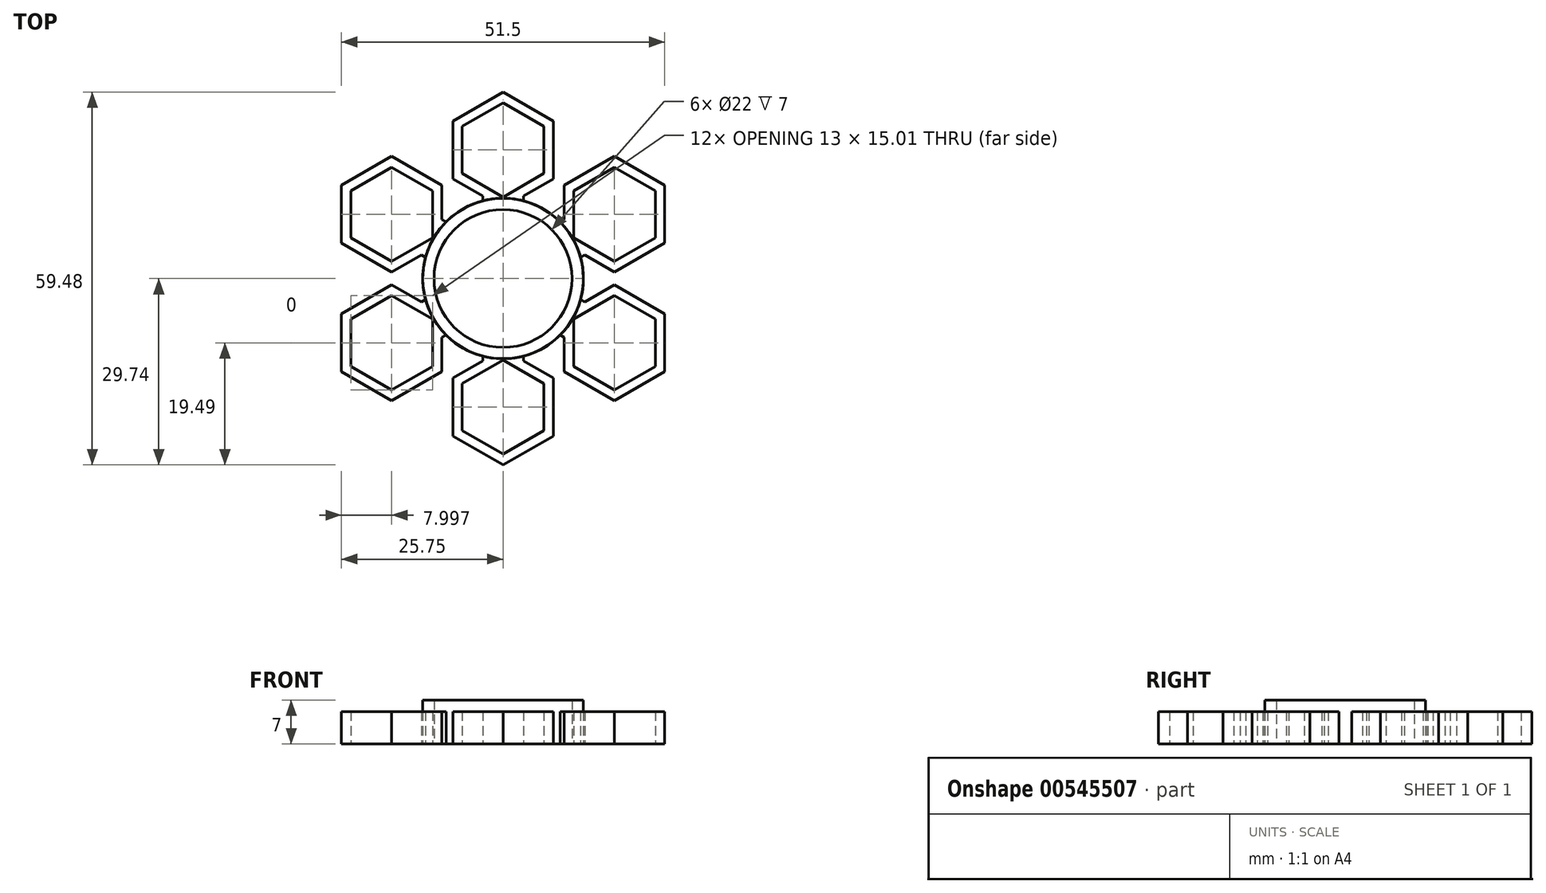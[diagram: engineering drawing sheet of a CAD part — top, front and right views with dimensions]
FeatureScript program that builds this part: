
annotation { "Feature Type Name" : "Feature", "Feature Type Description" : "" }
export const myFeature = defineFeature(function(context is Context, id is Id, definition is map)
    precondition{}
    {
        {
            var Q0;
            Q0=qCreatedBy(makeId("Top.planeOp"),FACE);
            var sketch = newSketch(context, id + "F0", { "sketchPlane" : qUnion([Q0])});
            skCircle(sketch, "E0", {"center": v(0, 0) * mm, "radius": 30 * mm});
            skCircle(sketch, "E1", {"center": v(0, 0) * mm, "radius": 11 * mm});
            skLineSegment(sketch, "E2", {"start": v(0, 20.5) * mm, "end": v(6.5, 20.5) * mm});
            skPoint(sketch, "E2.endSnap0", {"position": v(0, 20.5) * mm});
            skLineSegment(sketch, "E3", {"start": v(0, 20.5) * mm, "end": v(-6.5, 20.5) * mm});
            skCircle(sketch, "E4.cCircle", {"center": v(0, 20.5) * mm, "radius": 6.5 * mm, "construction": true});
            skLineSegment(sketch, "E4.0", {"start": v(-6.5, 16.75) * mm, "end": v(-6.5, 24.25) * mm});
            skLineSegment(sketch, "E4.1", {"start": v(-6.5, 24.25) * mm, "end": v(0, 28) * mm});
            skLineSegment(sketch, "E4.2", {"start": v(0, 28) * mm, "end": v(6.5, 24.25) * mm});
            skLineSegment(sketch, "E4.3", {"start": v(6.5, 24.25) * mm, "end": v(6.5, 16.75) * mm});
            skLineSegment(sketch, "E4.4", {"start": v(6.5, 16.75) * mm, "end": v(0, 13) * mm});
            skLineSegment(sketch, "E4.5", {"start": v(0, 13) * mm, "end": v(-6.5, 16.75) * mm});
            skPoint(sketch, "E4.0.midPoint", {"position": v(-6.5, 20.5) * mm});
            skLineSegment(sketch, "E5.MirrorCS", {"start": v(0, 35.51) * mm, "end": v(0, 28) * mm});
            skLineSegment(sketch, "E6.MirrorCS", {"start": v(6.5, -24.25) * mm, "end": v(6.5, -16.75) * mm});
            skLineSegment(sketch, "E7.MirrorCS", {"start": v(6.5, -16.75) * mm, "end": v(0, -13) * mm});
            skLineSegment(sketch, "E8.MirrorCS", {"start": v(0, -13) * mm, "end": v(-6.5, -16.75) * mm});
            skLineSegment(sketch, "E9.MirrorCS", {"start": v(-6.5, -16.75) * mm, "end": v(-6.5, -24.25) * mm});
            skLineSegment(sketch, "E10.MirrorCS", {"start": v(-6.5, -24.25) * mm, "end": v(0, -28) * mm});
            skLineSegment(sketch, "E11.MirrorCS", {"start": v(0, -28) * mm, "end": v(6.5, -24.25) * mm});
            skLineSegment(sketch, "E12", {"start": v(-3.25, 14.87) * mm, "end": v(-3.25, 10.5) * mm});
            skLineSegment(sketch, "E13", {"start": v(3.25, 13.14) * mm, "end": v(3.25, 12.38) * mm});
            skLineSegment(sketch, "E14", {"start": v(-3.25, -13.14) * mm, "end": v(-3.25, -12.38) * mm});
            skLineSegment(sketch, "E15", {"start": v(3.25, -13.14) * mm, "end": v(3.25, -12.38) * mm});
            skLineSegment(sketch, "E16.0", {"start": v(8, -15.88) * mm, "end": v(3.25, -13.14) * mm});
            skLineSegment(sketch, "E16.1", {"start": v(-8, -15.88) * mm, "end": v(-8, -25.12) * mm});
            skLineSegment(sketch, "E16.2", {"start": v(-8, -25.12) * mm, "end": v(0, -29.74) * mm});
            skLineSegment(sketch, "E16.4", {"start": v(0, -29.74) * mm, "end": v(8, -25.12) * mm});
            skLineSegment(sketch, "E16.5", {"start": v(8, -25.12) * mm, "end": v(8, -15.88) * mm});
            skLineSegment(sketch, "E17.0", {"start": v(-3.25, 13.14) * mm, "end": v(-8, 15.88) * mm});
            skLineSegment(sketch, "E17.1", {"start": v(-8, 25.12) * mm, "end": v(0, 29.74) * mm});
            skLineSegment(sketch, "E17.2", {"start": v(0, 29.74) * mm, "end": v(8, 25.12) * mm});
            skLineSegment(sketch, "E17.3", {"start": v(-8, 15.88) * mm, "end": v(-8, 25.12) * mm});
            skLineSegment(sketch, "E17.4", {"start": v(8, 25.12) * mm, "end": v(8, 15.88) * mm});
            skLineSegment(sketch, "E17.5", {"start": v(8, 15.88) * mm, "end": v(3.25, 13.14) * mm});
            skArc(sketch, "E18.0", {"start": v(-3.25, 12.38) * mm, "mid": v(-12.8, 0) * mm, "end": v(-3.25, -12.38) * mm});
            skArc(sketch, "E19.trimOffspring", {"start": v(3.25, -12.38) * mm, "mid": v(12.8, 0) * mm, "end": v(3.25, 12.38) * mm});
            skLineSegment(sketch, "E20.trimOffspring", {"start": v(-3.25, -13.14) * mm, "end": v(-8, -15.88) * mm});
            skPoint(sketch, "E21.orphan", {"position": v(-3.25, -14.87) * mm});
            skPoint(sketch, "E22.orphan", {"position": v(3.25, -14.87) * mm});
            skLineSegment(sketch, "E23.trimOffspring", {"start": v(0, 12.8) * mm, "end": v(0, 30) * mm});
            skPoint(sketch, "E24.start.orphan", {"position": v(0, 11) * mm});
            skPoint(sketch, "E25.orphan", {"position": v(3.25, 14.87) * mm});
            skSolve(sketch);
        }
        {
            var Q0;
            Q0=makeQuery(id+"F0.imprint","IMPRINT",FACE,{"disambiguationData":[TD([[makeQuery(id+"F0.imprint","IMPRINT",EDGE,{"derivedFrom":sQuery(id+"F0.wireOp",EDGE,"E1")}),-1.0]])]});
            var Q1;
            {var subQ5=sQuery(id+"F0.wireOp",EDGE,"E4.1");Q1=makeQuery(id+"F0.imprint","IMPRINT",FACE,{"disambiguationData":[TD([[makeQuery(id+"F0.imprint","IMPRINT",EDGE,{"derivedFrom":subQ5}),1.0]])]});}
            extrude(context, id + "F1", {"entities" : qUnion([Q0, Q1]), "depth" : 7 * mm, "offsetDistance" : 25 * mm});
        }
        {
            var Q0;
            Q0=makeQuery(id+"F1.opExtrude","CAP_FACE",FACE,{"disambiguationData":[OSD([sQuery(id+"F0.wireOp",EDGE,"E1"),sQuery(id+"F0.wireOp",EDGE,"E4.0"),sQuery(id+"F0.wireOp",EDGE,"E4.1"),sQuery(id+"F0.wireOp",EDGE,"E4.2"),sQuery(id+"F0.wireOp",EDGE,"E4.3"),sQuery(id+"F0.wireOp",EDGE,"E4.4"),sQuery(id+"F0.wireOp",EDGE,"E4.5"),sQuery(id+"F0.wireOp",EDGE,"E6.MirrorCS"),sQuery(id+"F0.wireOp",EDGE,"E7.MirrorCS"),sQuery(id+"F0.wireOp",EDGE,"E8.MirrorCS"),sQuery(id+"F0.wireOp",EDGE,"E9.MirrorCS"),sQuery(id+"F0.wireOp",EDGE,"E10.MirrorCS"),sQuery(id+"F0.wireOp",EDGE,"E11.MirrorCS"),sQuery(id+"F0.wireOp",EDGE,"E12"),sQuery(id+"F0.wireOp",EDGE,"E13"),sQuery(id+"F0.wireOp",EDGE,"E14"),sQuery(id+"F0.wireOp",EDGE,"E15"),sQuery(id+"F0.wireOp",EDGE,"E16.0"),sQuery(id+"F0.wireOp",EDGE,"E16.1"),sQuery(id+"F0.wireOp",EDGE,"E16.2"),sQuery(id+"F0.wireOp",EDGE,"E16.4"),sQuery(id+"F0.wireOp",EDGE,"E16.5"),sQuery(id+"F0.wireOp",EDGE,"E17.0"),sQuery(id+"F0.wireOp",EDGE,"E17.1"),sQuery(id+"F0.wireOp",EDGE,"E17.2"),sQuery(id+"F0.wireOp",EDGE,"E17.3"),sQuery(id+"F0.wireOp",EDGE,"E17.4"),sQuery(id+"F0.wireOp",EDGE,"E17.5"),sQuery(id+"F0.wireOp",EDGE,"E18.0"),sQuery(id+"F0.wireOp",EDGE,"E19.trimOffspring"),sQuery(id+"F0.wireOp",EDGE,"E20.trimOffspring")])],"isStart":false});
            var sketch = newSketch(context, id + "F2", { "sketchPlane" : qUnion([Q0])});
            skArc(sketch, "E26", {"start": v(-3.25, 12.38) * mm, "mid": v(0, 12.8) * mm, "end": v(3.25, 12.38) * mm});
            skLineSegment(sketch, "E27", {"start": v(-3.25, 12.38) * mm, "end": v(-3.25, 13.14) * mm});
            skLineSegment(sketch, "E28", {"start": v(-3.25, 13.14) * mm, "end": v(-8, 15.88) * mm});
            skLineSegment(sketch, "E29", {"start": v(-8, 15.88) * mm, "end": v(-8, 25.12) * mm});
            skLineSegment(sketch, "E30", {"start": v(-8, 25.12) * mm, "end": v(0, 29.74) * mm});
            skLineSegment(sketch, "E31", {"start": v(0, 29.74) * mm, "end": v(8, 25.12) * mm});
            skLineSegment(sketch, "E32", {"start": v(8, 25.12) * mm, "end": v(8, 15.88) * mm});
            skLineSegment(sketch, "E33", {"start": v(8, 15.88) * mm, "end": v(3.25, 13.14) * mm});
            skLineSegment(sketch, "E34", {"start": v(3.25, 13.14) * mm, "end": v(3.25, 12.38) * mm});
            skLineSegment(sketch, "E35", {"start": v(0, 13) * mm, "end": v(-6.5, 16.75) * mm});
            skLineSegment(sketch, "E36", {"start": v(-6.5, 16.75) * mm, "end": v(-6.5, 24.25) * mm});
            skLineSegment(sketch, "E37", {"start": v(-6.5, 24.25) * mm, "end": v(0, 28) * mm});
            skLineSegment(sketch, "E38", {"start": v(0, 28) * mm, "end": v(6.5, 24.25) * mm});
            skLineSegment(sketch, "E39", {"start": v(6.5, 24.25) * mm, "end": v(6.5, 16.75) * mm});
            skLineSegment(sketch, "E40", {"start": v(6.5, 16.75) * mm, "end": v(0, 13) * mm});
            skArc(sketch, "E41", {"start": v(-3.25, -12.38) * mm, "mid": v(0, -12.8) * mm, "end": v(3.25, -12.38) * mm});
            skLineSegment(sketch, "E42", {"start": v(3.25, -12.38) * mm, "end": v(3.25, -13.14) * mm});
            skLineSegment(sketch, "E43", {"start": v(3.25, -13.14) * mm, "end": v(8, -15.88) * mm});
            skLineSegment(sketch, "E44", {"start": v(8, -15.88) * mm, "end": v(8, -25.12) * mm});
            skLineSegment(sketch, "E45", {"start": v(8, -25.12) * mm, "end": v(0, -29.74) * mm});
            skLineSegment(sketch, "E46", {"start": v(0, -29.74) * mm, "end": v(-8, -25.12) * mm});
            skLineSegment(sketch, "E47", {"start": v(-8, -25.12) * mm, "end": v(-8, -15.88) * mm});
            skLineSegment(sketch, "E48", {"start": v(-8, -15.88) * mm, "end": v(-3.25, -13.14) * mm});
            skLineSegment(sketch, "E49", {"start": v(-3.25, -13.14) * mm, "end": v(-3.25, -12.38) * mm});
            skLineSegment(sketch, "E50", {"start": v(0, -13) * mm, "end": v(-6.5, -16.75) * mm});
            skLineSegment(sketch, "E51", {"start": v(-6.5, -16.75) * mm, "end": v(-6.5, -24.25) * mm});
            skLineSegment(sketch, "E52", {"start": v(-6.5, -24.25) * mm, "end": v(0, -28) * mm});
            skLineSegment(sketch, "E53", {"start": v(0, -28) * mm, "end": v(6.5, -24.25) * mm});
            skLineSegment(sketch, "E54", {"start": v(6.5, -24.25) * mm, "end": v(6.5, -16.75) * mm});
            skLineSegment(sketch, "E55", {"start": v(6.5, -16.75) * mm, "end": v(0, -13) * mm});
            skSolve(sketch);
        }
        {
            var Q0;
            Q0 = qSketchRegion(id + "F2", true);
            extrude(context, id + "F3", {"entities" : qUnion([Q0]), "operationType" : NewBodyOperationType.REMOVE, "oppositeDirection" : true, "depth" : 1.83 * mm, "offsetDistance" : 25 * mm});
        }
        {
            var Q0;
            Q0=makeQuery(id+"F1.opExtrude","SWEPT_BODY",BODY,{"disambiguationData":[OSD([sQuery(id+"F0.wireOp",EDGE,"E1"),sQuery(id+"F0.wireOp",EDGE,"E4.0"),sQuery(id+"F0.wireOp",EDGE,"E4.1"),sQuery(id+"F0.wireOp",EDGE,"E4.2"),sQuery(id+"F0.wireOp",EDGE,"E4.3"),sQuery(id+"F0.wireOp",EDGE,"E4.4"),sQuery(id+"F0.wireOp",EDGE,"E4.5"),sQuery(id+"F0.wireOp",EDGE,"E6.MirrorCS"),sQuery(id+"F0.wireOp",EDGE,"E7.MirrorCS"),sQuery(id+"F0.wireOp",EDGE,"E8.MirrorCS"),sQuery(id+"F0.wireOp",EDGE,"E9.MirrorCS"),sQuery(id+"F0.wireOp",EDGE,"E10.MirrorCS"),sQuery(id+"F0.wireOp",EDGE,"E11.MirrorCS"),sQuery(id+"F0.wireOp",EDGE,"E12"),sQuery(id+"F0.wireOp",EDGE,"E13"),sQuery(id+"F0.wireOp",EDGE,"E14"),sQuery(id+"F0.wireOp",EDGE,"E15"),sQuery(id+"F0.wireOp",EDGE,"E16.0"),sQuery(id+"F0.wireOp",EDGE,"E16.1"),sQuery(id+"F0.wireOp",EDGE,"E16.2"),sQuery(id+"F0.wireOp",EDGE,"E16.4"),sQuery(id+"F0.wireOp",EDGE,"E16.5"),sQuery(id+"F0.wireOp",EDGE,"E17.0"),sQuery(id+"F0.wireOp",EDGE,"E17.1"),sQuery(id+"F0.wireOp",EDGE,"E17.2"),sQuery(id+"F0.wireOp",EDGE,"E17.3"),sQuery(id+"F0.wireOp",EDGE,"E17.4"),sQuery(id+"F0.wireOp",EDGE,"E17.5"),sQuery(id+"F0.wireOp",EDGE,"E18.0"),sQuery(id+"F0.wireOp",EDGE,"E19.trimOffspring"),sQuery(id+"F0.wireOp",EDGE,"E20.trimOffspring")])]});
            var Q1;
            Q1=makeQuery(id+"F3.boolean.opBoolean","MERGE",FACE,{"derivedFrom":[makeQuery(id+"F1.opExtrude","SWEPT_FACE",FACE,{"disambiguationData":[OSD([sQuery(id+"F0.wireOp",EDGE,"E18.0")])]}),makeQuery(id+"F1.opExtrude","SWEPT_FACE",FACE,{"disambiguationData":[OSD([sQuery(id+"F0.wireOp",EDGE,"E19.trimOffspring")])]}),makeQuery(id+"F3.opExtrude","SWEPT_FACE",FACE,{"disambiguationData":[OSD([sQuery(id+"F2.wireOp",EDGE,"E26")])]}),makeQuery(id+"F3.opExtrude","SWEPT_FACE",FACE,{"disambiguationData":[OSD([sQuery(id+"F2.wireOp",EDGE,"E41")])]})]});
            circularPattern(context, id + "F4", {"entities" : qUnion([Q0]), "axis" : qUnion([Q1]), "angle" : 360 * degree, "instanceCount" : 6, "equalSpace" : true});
        }
    });
